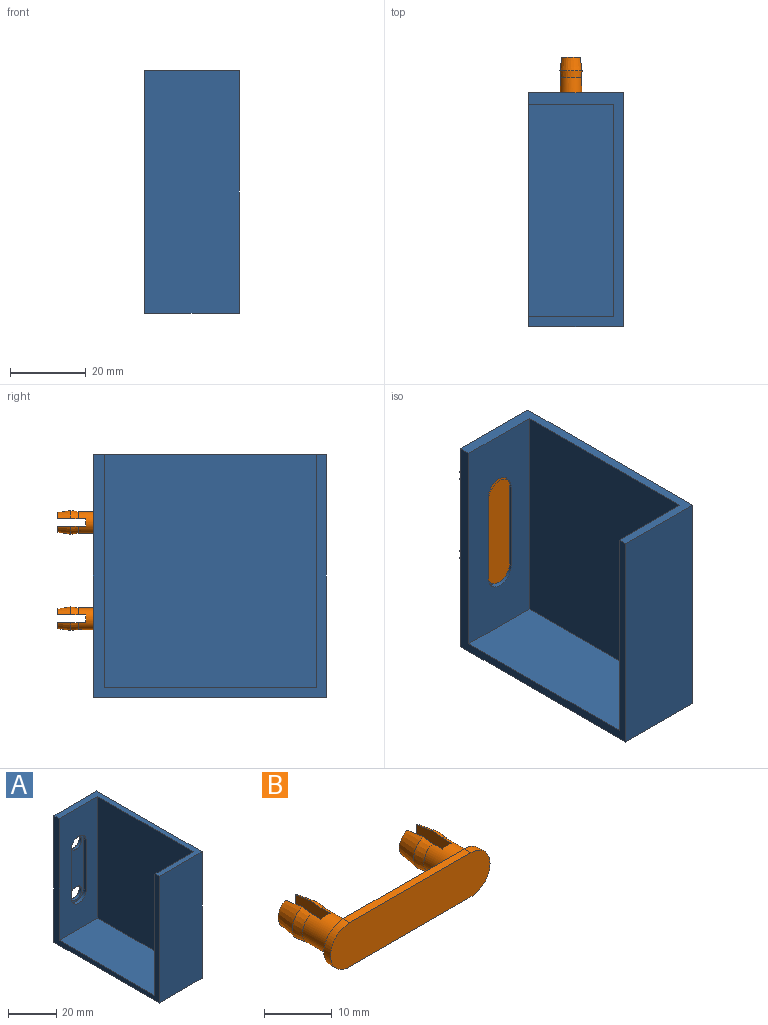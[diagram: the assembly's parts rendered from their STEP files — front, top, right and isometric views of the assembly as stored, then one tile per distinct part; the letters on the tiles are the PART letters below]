
ASSEMBLY  parts=2 mates=1
PART A: 17 faces, bbox 25x61.5x64 mm
  f0: plane 61.5x22.5mm, normal (0,-1,0), area 1111.1mm2, adj f1,f2,f7,f8,f10,f11,f12,f13
  f1: plane 61.5x25mm, normal (0,0,1), area 277.5mm2, adj f0,f2,f3,f4,f6,f7,f16
  f2: plane 64x61.5mm, normal (-1,0,0), area 492mm2, adj f0,f1,f3,f5,f6,f8,f16
  f3: plane 64x25mm, normal (0,-1,0), area 1600mm2, adj f1,f2,f4,f5
  f4: plane 64x61.5mm, normal (1,0,0), area 3936mm2, adj f1,f3,f5,f16
  f5: plane 61.5x25mm, normal (0,0,-1), area 1537.5mm2, adj f2,f3,f4,f16
  f6: plane 61.5x22.5mm, normal (0,1,0), area 1383.8mm2, adj f1,f2,f7,f8
  f7: plane 61.5x56mm, normal (-1,0,0), area 3444mm2, adj f0,f1,f6,f8
  f8: plane 56x22.5mm, normal (0,0,1), area 1260mm2, adj f0,f2,f6,f7
  f9: plane 33.9x8.5mm, normal (0,-1,0), area 206.3mm2, adj f10,f11,f12,f13,f14,f15
  f10: cylinder r=4.25mm len=8.5mm, axis (0,-1,0), area 21.4mm2, adj f0,f9,f11,f13
  f11: plane 25.4x1.6mm, normal (-1,0,0), area 40.6mm2, adj f0,f9,f10,f12
  f12: cylinder r=4.25mm len=8.5mm, axis (0,-1,0), area 21.4mm2, adj f0,f9,f11,f13
  f13: plane 25.4x1.6mm, normal (1,0,0), area 40.6mm2, adj f0,f9,f10,f12
  f14: cylinder r=3.25mm len=6.5mm, axis (0,1,0), area 28.6mm2, adj f9,f16
  f15: cylinder r=3.25mm len=6.5mm, axis (0,1,0), area 28.6mm2, adj f9,f16
  f16: plane 64x25mm, normal (0,1,0), area 1533.6mm2, adj f1,f2,f4,f5,f14,f15
PART B: 26 faces, bbox 33.4x12.4x8 mm
  f0: cylinder r=2.85mm len=5.7mm, axis (0,-1,0), area 92.1mm2, adj f7,f12,f19,f20,f21,f22
  f1: cylinder r=2.85mm len=5.7mm, axis (0,-1,0), area 92.1mm2, adj f4,f12,f16,f23,f24,f25
  f2: plane 4.8x1.6mm, normal (0,1,0), area 5.5mm2, adj f15,f25
  f3: cone r=3.1mm half-angle=8.1deg, axis (0,-1,0), area 24.4mm2, adj f4,f14,f24
  f4: cone r=2.85mm half-angle=7.5deg, axis (0,1,0), area 14mm2, adj f1,f3,f24
  f5: plane 4.8x1.6mm, normal (0,1,0), area 5.5mm2, adj f18,f22
  f6: cone r=3.1mm half-angle=8.1deg, axis (0,-1,0), area 24.4mm2, adj f7,f17,f21
  f7: cone r=2.85mm half-angle=7.5deg, axis (0,1,0), area 14mm2, adj f0,f6,f21
  f8: cylinder r=4mm len=8mm, axis (0,-1,0), area 17.6mm2, adj f9,f11,f12,f13
  f9: plane 25.4x1.4mm, normal (0,0,-1), area 35.6mm2, adj f8,f10,f12,f13
  f10: cylinder r=4mm len=8mm, axis (0,-1,0), area 17.6mm2, adj f9,f11,f12,f13
  f11: plane 25.4x1.4mm, normal (0,0,1), area 35.6mm2, adj f8,f10,f12,f13
  f12: plane 33.4x8mm, normal (0,1,0), area 202.4mm2, adj f0,f1,f8,f9,f10,f11
  f13: plane 33.4x8mm, normal (0,-1,0), area 253.5mm2, adj f8,f9,f10,f11
  f14: plane 4.8x1.6mm, normal (0,1,0), area 5.5mm2, adj f3,f24
  f15: cone r=3.1mm half-angle=8.1deg, axis (0,-1,0), area 24.4mm2, adj f2,f16,f25
  f16: cone r=2.85mm half-angle=7.5deg, axis (0,1,0), area 14mm2, adj f1,f15,f25
  f17: plane 4.8x1.6mm, normal (0,1,0), area 5.5mm2, adj f6,f21
  f18: cone r=3.1mm half-angle=8.1deg, axis (0,-1,0), area 24.4mm2, adj f5,f19,f22
  f19: cone r=2.85mm half-angle=7.5deg, axis (0,1,0), area 14mm2, adj f0,f18,f22
  f20: plane 5.7x2mm, normal (0,1,0), area 11.2mm2, adj f0,f21,f22
  f21: plane 7.42x5.89mm, normal (1,0,0), area 40mm2, adj f0,f6,f7,f17,f20
  f22: plane 7.42x5.89mm, normal (-1,0,0), area 40mm2, adj f0,f5,f18,f19,f20
  f23: plane 5.7x2mm, normal (0,1,0), area 11.2mm2, adj f1,f24,f25
  f24: plane 7.42x5.89mm, normal (1,0,0), area 40mm2, adj f1,f3,f4,f14,f23
  f25: plane 7.42x5.89mm, normal (-1,0,0), area 40mm2, adj f1,f2,f15,f16,f23
PLACE A t=(0,-1.4,0)mm
PLACE B rot(axis=(0,1,0),90deg) t=(-33.06,26.6,33.43)mm
MATE fastened A.f0 <-> B.f13  axis (0,-1,0) through (-1.31,26.6,33.43)mm
